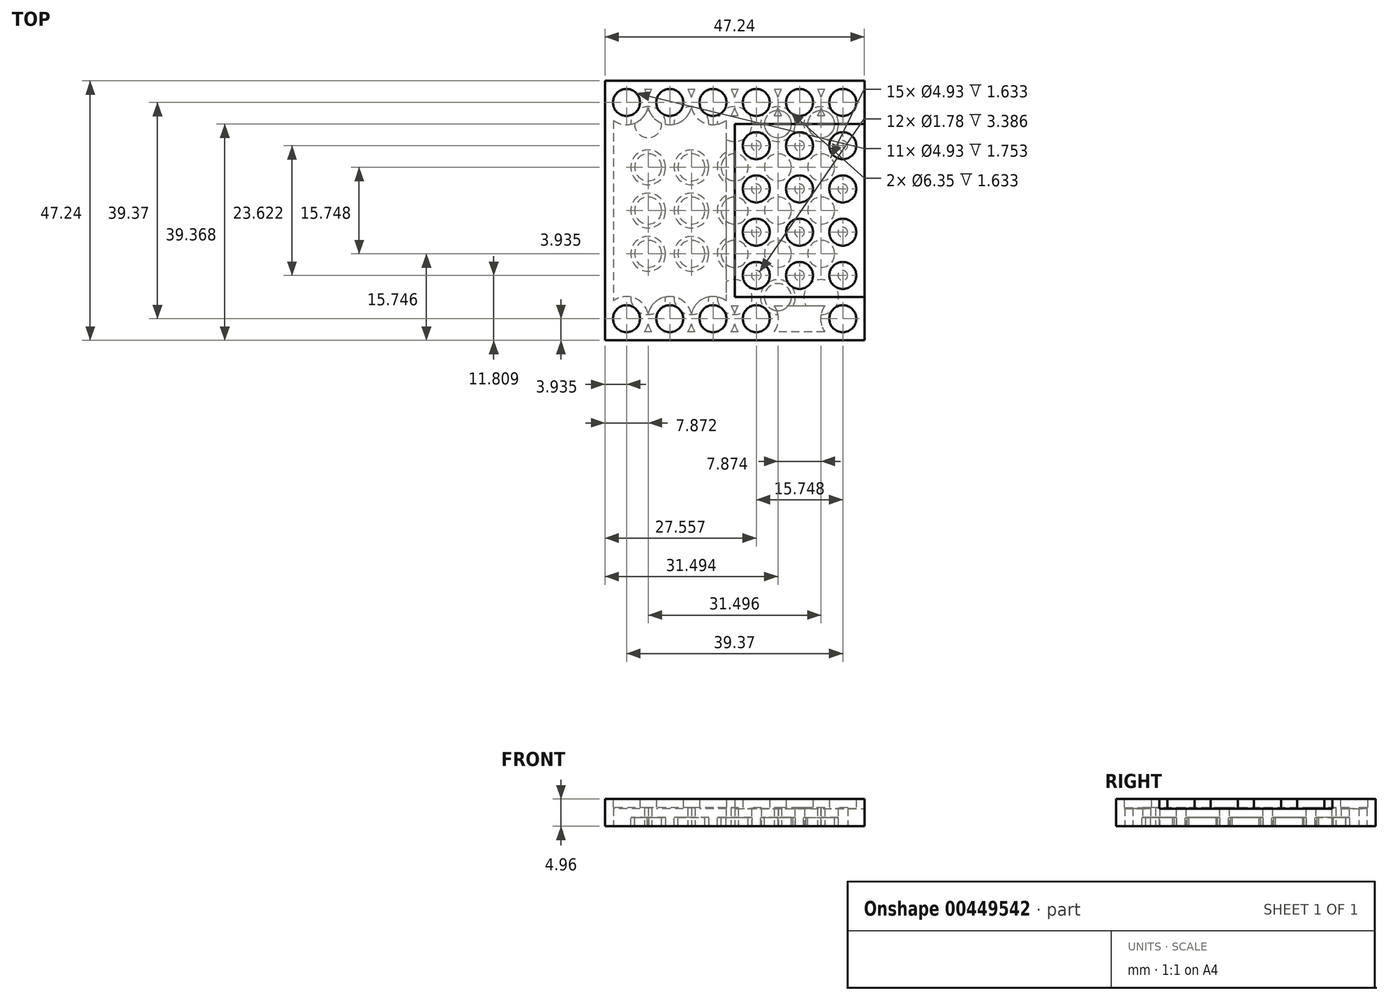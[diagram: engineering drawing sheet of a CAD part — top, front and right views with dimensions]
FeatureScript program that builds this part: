
annotation { "Feature Type Name" : "Feature", "Feature Type Description" : "" }
export const myFeature = defineFeature(function(context is Context, id is Id, definition is map)
    precondition{}
    {
        {
            var Q0;
            Q0=qCreatedBy(makeId("Top.planeOp"),FACE);
            var sketch = newSketch(context, id + "F0", { "sketchPlane" : qUnion([Q0])});
            skLineSegment(sketch, "E0.rect.bottom", {"start": v(23.62, 23.62) * mm, "end": v(-23.62, 23.62) * mm});
            skLineSegment(sketch, "E0.rect.top", {"start": v(23.62, -23.62) * mm, "end": v(-23.62, -23.62) * mm});
            skLineSegment(sketch, "E0.rect.left", {"start": v(23.62, 23.62) * mm, "end": v(23.62, -23.62) * mm});
            skLineSegment(sketch, "E0.rect.right", {"start": v(-23.62, 23.62) * mm, "end": v(-23.62, -23.62) * mm});
            skPoint(sketch, "E0.rect.middle", {"position": v(0, 0) * mm});
            skSolve(sketch);
        }
        {
            var Q0;
            Q0=makeQuery(id+"F0.imprint","IMPRINT",FACE,{"disambiguationData":[TD([[makeQuery(id+"F0.imprint","IMPRINT",EDGE,{"derivedFrom":sQuery(id+"F0.wireOp",EDGE,"E0.rect.bottom")}),1.0]])]});
            extrude(context, id + "F1", {"entities" : qUnion([Q0]), "depth" : 3.2 * mm});
        }
        {
            var Q0;
            Q0=makeQuery(id+"F1.opExtrude","CAP_FACE",FACE,{"disambiguationData":[OSD([sQuery(id+"F0.wireOp",EDGE,"E0.rect.bottom"),sQuery(id+"F0.wireOp",EDGE,"E0.rect.top"),sQuery(id+"F0.wireOp",EDGE,"E0.rect.left"),sQuery(id+"F0.wireOp",EDGE,"E0.rect.right")])],"isStart":false});
            var sketch = newSketch(context, id + "F2", { "sketchPlane" : qUnion([Q0])});
            skLineSegment(sketch, "E1", {"start": v(0, 0) * mm, "end": v(0, 7.87) * mm});
            skLineSegment(sketch, "E2", {"start": v(0, 7.87) * mm, "end": v(0, 15.75) * mm});
            skLineSegment(sketch, "E3", {"start": v(0, 0) * mm, "end": v(0, -7.87) * mm});
            skLineSegment(sketch, "E4", {"start": v(0, -7.87) * mm, "end": v(0, -15.75) * mm});
            skPoint(sketch, "E4.endSnap0", {"position": v(0, -23.62) * mm});
            skLineSegment(sketch, "E5", {"start": v(0, 0) * mm, "end": v(3.94, 0) * mm});
            skLineSegment(sketch, "E6", {"start": v(3.94, 0) * mm, "end": v(11.81, 0) * mm});
            skLineSegment(sketch, "E7", {"start": v(11.81, 0) * mm, "end": v(19.69, 0) * mm});
            skLineSegment(sketch, "E8", {"start": v(0, 0) * mm, "end": v(-3.94, 0) * mm});
            skLineSegment(sketch, "E9", {"start": v(-3.94, 0) * mm, "end": v(-11.81, 0) * mm});
            skLineSegment(sketch, "E10", {"start": v(-11.81, 0) * mm, "end": v(-19.69, 0) * mm});
            skLineSegment(sketch, "E11", {"start": v(-19.69, 0) * mm, "end": v(-19.69, -3.94) * mm});
            skLineSegment(sketch, "E12", {"start": v(-19.69, -3.94) * mm, "end": v(-19.69, -11.81) * mm});
            skLineSegment(sketch, "E13", {"start": v(-19.69, 0) * mm, "end": v(-19.69, 3.94) * mm});
            skLineSegment(sketch, "E14", {"start": v(-19.69, 3.94) * mm, "end": v(-19.69, 11.81) * mm});
            skLineSegment(sketch, "E15", {"start": v(-19.69, 3.94) * mm, "end": v(-11.81, 3.94) * mm});
            skLineSegment(sketch, "E16", {"start": v(-11.81, 3.94) * mm, "end": v(-3.94, 3.94) * mm});
            skLineSegment(sketch, "E17", {"start": v(-3.94, 3.94) * mm, "end": v(-3.94, 11.81) * mm});
            skLineSegment(sketch, "E18", {"start": v(-3.94, 11.81) * mm, "end": v(-11.81, 11.81) * mm});
            skLineSegment(sketch, "E19", {"start": v(-19.69, -3.94) * mm, "end": v(-11.81, -3.94) * mm});
            skLineSegment(sketch, "E20", {"start": v(-11.81, -3.94) * mm, "end": v(-3.94, -3.94) * mm});
            skLineSegment(sketch, "E21", {"start": v(-3.94, -3.94) * mm, "end": v(-3.94, -11.81) * mm});
            skLineSegment(sketch, "E22", {"start": v(-3.94, -11.81) * mm, "end": v(-11.81, -11.81) * mm});
            skLineSegment(sketch, "E23", {"start": v(3.94, 0) * mm, "end": v(3.94, 3.94) * mm});
            skPoint(sketch, "E23.endSnap0", {"position": v(0, 3.94) * mm});
            skLineSegment(sketch, "E24", {"start": v(3.94, 3.94) * mm, "end": v(3.94, 11.81) * mm});
            skPoint(sketch, "E24.endSnap0", {"position": v(0, 11.81) * mm});
            skLineSegment(sketch, "E25", {"start": v(3.94, 11.81) * mm, "end": v(11.81, 11.81) * mm});
            skLineSegment(sketch, "E26", {"start": v(11.81, 11.81) * mm, "end": v(19.69, 11.81) * mm});
            skLineSegment(sketch, "E27", {"start": v(19.69, 11.81) * mm, "end": v(19.69, 3.94) * mm});
            skLineSegment(sketch, "E28", {"start": v(19.69, 3.94) * mm, "end": v(11.81, 3.94) * mm});
            skLineSegment(sketch, "E29", {"start": v(3.94, 0) * mm, "end": v(3.94, -3.94) * mm});
            skPoint(sketch, "E29.endSnap0", {"position": v(0, -3.94) * mm});
            skLineSegment(sketch, "E30", {"start": v(3.94, -3.94) * mm, "end": v(3.94, -11.81) * mm});
            skPoint(sketch, "E30.endSnap0", {"position": v(0, -11.81) * mm});
            skLineSegment(sketch, "E31", {"start": v(3.94, -11.81) * mm, "end": v(11.81, -11.81) * mm});
            skLineSegment(sketch, "E32", {"start": v(11.81, -11.81) * mm, "end": v(19.69, -11.81) * mm});
            skLineSegment(sketch, "E33", {"start": v(19.69, -11.81) * mm, "end": v(19.69, -3.94) * mm});
            skLineSegment(sketch, "E34", {"start": v(19.69, -3.94) * mm, "end": v(11.81, -3.94) * mm});
            skCircle(sketch, "E35", {"center": v(-19.69, 11.81) * mm, "radius": 2.46 * mm});
            skCircle(sketch, "E36", {"center": v(-11.81, 11.81) * mm, "radius": 2.46 * mm});
            skCircle(sketch, "E37", {"center": v(-3.94, 11.81) * mm, "radius": 2.46 * mm});
            skCircle(sketch, "E38", {"center": v(3.94, 11.81) * mm, "radius": 2.46 * mm});
            skCircle(sketch, "E39", {"center": v(11.81, 11.81) * mm, "radius": 2.46 * mm});
            skCircle(sketch, "E40", {"center": v(19.69, 11.81) * mm, "radius": 2.46 * mm});
            skCircle(sketch, "E41", {"center": v(19.69, 3.94) * mm, "radius": 2.46 * mm});
            skCircle(sketch, "E42", {"center": v(11.81, 3.94) * mm, "radius": 2.46 * mm});
            skCircle(sketch, "E43", {"center": v(3.94, 3.94) * mm, "radius": 2.46 * mm});
            skCircle(sketch, "E44", {"center": v(-3.94, 3.94) * mm, "radius": 2.46 * mm});
            skCircle(sketch, "E45", {"center": v(-11.81, 3.94) * mm, "radius": 2.46 * mm});
            skCircle(sketch, "E46", {"center": v(-19.69, 3.94) * mm, "radius": 2.46 * mm});
            skCircle(sketch, "E47", {"center": v(-19.69, -3.94) * mm, "radius": 2.46 * mm});
            skCircle(sketch, "E48", {"center": v(-11.81, -3.94) * mm, "radius": 2.46 * mm});
            skCircle(sketch, "E49", {"center": v(-3.94, -3.94) * mm, "radius": 2.46 * mm});
            skCircle(sketch, "E50", {"center": v(-3.94, -11.81) * mm, "radius": 2.46 * mm});
            skCircle(sketch, "E51", {"center": v(-11.81, -11.81) * mm, "radius": 2.46 * mm});
            skCircle(sketch, "E52", {"center": v(-19.69, -11.81) * mm, "radius": 2.46 * mm});
            skCircle(sketch, "E53", {"center": v(3.94, -11.81) * mm, "radius": 2.46 * mm});
            skCircle(sketch, "E54", {"center": v(11.81, -11.81) * mm, "radius": 2.46 * mm});
            skCircle(sketch, "E55", {"center": v(19.69, -11.81) * mm, "radius": 2.46 * mm});
            skCircle(sketch, "E56", {"center": v(19.69, -3.94) * mm, "radius": 2.46 * mm});
            skCircle(sketch, "E57", {"center": v(11.81, -3.94) * mm, "radius": 2.46 * mm});
            skCircle(sketch, "E58", {"center": v(3.94, -3.94) * mm, "radius": 2.46 * mm});
            skLineSegment(sketch, "E59", {"start": v(0, -15.75) * mm, "end": v(23.62, -15.75) * mm});
            skLineSegment(sketch, "E60.MirrorCS", {"start": v(3.94, -19.69) * mm, "end": v(11.81, -19.69) * mm});
            skCircle(sketch, "E61.MirrorC", {"center": v(-11.81, -19.68) * mm, "radius": 2.46 * mm});
            skPoint(sketch, "E62.MirrorP", {"position": v(0, -19.69) * mm});
            skCircle(sketch, "E63.MirrorC", {"center": v(-3.94, -19.69) * mm, "radius": 2.46 * mm});
            skCircle(sketch, "E64.MirrorC", {"center": v(11.81, -19.69) * mm, "radius": 2.46 * mm});
            skLineSegment(sketch, "E65.MirrorCS", {"start": v(11.81, -19.69) * mm, "end": v(19.69, -19.69) * mm});
            skLineSegment(sketch, "E66.MirrorCS", {"start": v(-3.94, -19.68) * mm, "end": v(-11.81, -19.68) * mm});
            skCircle(sketch, "E67.MirrorC", {"center": v(19.69, -19.69) * mm, "radius": 2.46 * mm});
            skCircle(sketch, "E68.MirrorC", {"center": v(3.94, -19.69) * mm, "radius": 2.46 * mm});
            skCircle(sketch, "E69.MirrorC", {"center": v(-19.69, -19.69) * mm, "radius": 2.46 * mm});
            skLineSegment(sketch, "E70", {"start": v(0, 15.75) * mm, "end": v(23.62, 15.75) * mm});
            skCircle(sketch, "E71.MirrorC", {"center": v(-3.94, 19.69) * mm, "radius": 2.46 * mm});
            skCircle(sketch, "E72.MirrorC", {"center": v(3.94, 19.69) * mm, "radius": 2.46 * mm});
            skCircle(sketch, "E73.MirrorC", {"center": v(-11.81, 19.69) * mm, "radius": 2.46 * mm});
            skCircle(sketch, "E74.MirrorC", {"center": v(11.81, 19.69) * mm, "radius": 2.46 * mm});
            skCircle(sketch, "E75.MirrorC", {"center": v(-19.69, 19.69) * mm, "radius": 2.46 * mm});
            skPoint(sketch, "E76.MirrorP", {"position": v(0, 19.69) * mm});
            skCircle(sketch, "E77.MirrorC", {"center": v(19.69, 19.69) * mm, "radius": 2.46 * mm});
            skSolve(sketch);
        }
        {
            var Q0;
            Q0=makeQuery(id+"F2.imprint","IMPRINT",FACE,{"disambiguationData":[TD([[makeQuery(id+"F2.imprint","IMPRINT",EDGE,{"derivedFrom":sQuery(id+"F2.wireOp",EDGE,"E35")}),1.0]])]});
            var Q1;
            Q1=makeQuery(id+"F2.imprint","IMPRINT",FACE,{"disambiguationData":[TD([[makeQuery(id+"F2.imprint","IMPRINT",EDGE,{"derivedFrom":sQuery(id+"F2.wireOp",EDGE,"E36")}),1.0]])]});
            var Q2;
            {var subQ0=sQuery(id+"F2.wireOp",EDGE,"E18");var subQ1=sQuery(id+"F2.wireOp",EDGE,"E17");var subQ2=makeQuery(id+"F2.imprint","INTERSECT",VERTEX,{"derivedFrom":[subQ1,subQ0]});Q2=makeQuery(id+"F2.imprint","IMPRINT",FACE,{"disambiguationData":[TD([[makeQuery(id+"F2.imprint","IMPRINT",EDGE,{"disambiguationData":[TD([[subQ2,1.0]])],"derivedFrom":subQ1}),-1.0]])]});}
            var Q3;
            {var subQ0=sQuery(id+"F2.wireOp",EDGE,"E18");var subQ1=sQuery(id+"F2.wireOp",EDGE,"E17");var subQ2=makeQuery(id+"F2.imprint","INTERSECT",VERTEX,{"derivedFrom":[subQ1,subQ0]});Q3=makeQuery(id+"F2.imprint","IMPRINT",FACE,{"disambiguationData":[TD([[makeQuery(id+"F2.imprint","IMPRINT",EDGE,{"disambiguationData":[TD([[subQ2,1.0]])],"derivedFrom":subQ1}),1.0]])]});}
            var Q4;
            {var subQ0=sQuery(id+"F2.wireOp",EDGE,"E25");var subQ1=sQuery(id+"F2.wireOp",EDGE,"E24");var subQ2=makeQuery(id+"F2.imprint","INTERSECT",VERTEX,{"derivedFrom":[subQ1,subQ0]});Q4=makeQuery(id+"F2.imprint","IMPRINT",FACE,{"disambiguationData":[TD([[makeQuery(id+"F2.imprint","IMPRINT",EDGE,{"disambiguationData":[TD([[subQ2,1.0]])],"derivedFrom":subQ1}),1.0]])]});}
            var Q5;
            {var subQ0=sQuery(id+"F2.wireOp",EDGE,"E25");var subQ1=sQuery(id+"F2.wireOp",EDGE,"E24");var subQ2=makeQuery(id+"F2.imprint","INTERSECT",VERTEX,{"derivedFrom":[subQ1,subQ0]});Q5=makeQuery(id+"F2.imprint","IMPRINT",FACE,{"disambiguationData":[TD([[makeQuery(id+"F2.imprint","IMPRINT",EDGE,{"disambiguationData":[TD([[subQ2,1.0]])],"derivedFrom":subQ1}),-1.0]])]});}
            var Q6;
            {var subQ0=sQuery(id+"F2.wireOp",EDGE,"E24");var subQ1=sQuery(id+"F2.wireOp",EDGE,"E23");var subQ2=makeQuery(id+"F2.imprint","INTERSECT",VERTEX,{"derivedFrom":[subQ1,subQ0]});Q6=makeQuery(id+"F2.imprint","IMPRINT",FACE,{"disambiguationData":[TD([[makeQuery(id+"F2.imprint","IMPRINT",EDGE,{"disambiguationData":[TD([[subQ2,1.0]])],"derivedFrom":subQ1}),-1.0]])]});}
            var Q7;
            {var subQ0=sQuery(id+"F2.wireOp",EDGE,"E24");var subQ1=sQuery(id+"F2.wireOp",EDGE,"E23");var subQ2=makeQuery(id+"F2.imprint","INTERSECT",VERTEX,{"derivedFrom":[subQ1,subQ0]});Q7=makeQuery(id+"F2.imprint","IMPRINT",FACE,{"disambiguationData":[TD([[makeQuery(id+"F2.imprint","IMPRINT",EDGE,{"disambiguationData":[TD([[subQ2,1.0]])],"derivedFrom":subQ1}),1.0]])]});}
            var Q8;
            {var subQ0=sQuery(id+"F2.wireOp",EDGE,"E17");var subQ1=sQuery(id+"F2.wireOp",EDGE,"E16");var subQ2=makeQuery(id+"F2.imprint","INTERSECT",VERTEX,{"derivedFrom":[subQ1,subQ0]});Q8=makeQuery(id+"F2.imprint","IMPRINT",FACE,{"disambiguationData":[TD([[makeQuery(id+"F2.imprint","IMPRINT",EDGE,{"disambiguationData":[TD([[subQ2,1.0]])],"derivedFrom":subQ1}),-1.0]])]});}
            var Q9;
            {var subQ0=sQuery(id+"F2.wireOp",EDGE,"E17");var subQ1=sQuery(id+"F2.wireOp",EDGE,"E16");var subQ2=makeQuery(id+"F2.imprint","INTERSECT",VERTEX,{"derivedFrom":[subQ1,subQ0]});Q9=makeQuery(id+"F2.imprint","IMPRINT",FACE,{"disambiguationData":[TD([[makeQuery(id+"F2.imprint","IMPRINT",EDGE,{"disambiguationData":[TD([[subQ2,1.0]])],"derivedFrom":subQ1}),1.0]])]});}
            var Q10;
            {var subQ0=sQuery(id+"F2.wireOp",EDGE,"E16");var subQ1=sQuery(id+"F2.wireOp",EDGE,"E15");var subQ2=makeQuery(id+"F2.imprint","INTERSECT",VERTEX,{"derivedFrom":[subQ1,subQ0]});Q10=makeQuery(id+"F2.imprint","IMPRINT",FACE,{"disambiguationData":[TD([[makeQuery(id+"F2.imprint","IMPRINT",EDGE,{"disambiguationData":[TD([[subQ2,1.0]])],"derivedFrom":subQ1}),1.0]])]});}
            var Q11;
            {var subQ0=sQuery(id+"F2.wireOp",EDGE,"E16");var subQ1=sQuery(id+"F2.wireOp",EDGE,"E15");var subQ2=makeQuery(id+"F2.imprint","INTERSECT",VERTEX,{"derivedFrom":[subQ1,subQ0]});Q11=makeQuery(id+"F2.imprint","IMPRINT",FACE,{"disambiguationData":[TD([[makeQuery(id+"F2.imprint","IMPRINT",EDGE,{"disambiguationData":[TD([[subQ2,1.0]])],"derivedFrom":subQ1}),-1.0]])]});}
            var Q12;
            {var subQ1=sQuery(id+"F2.wireOp",EDGE,"E14");var subQ3=sQuery(id+"F2.wireOp",EDGE,"E46");var subQ4=makeQuery(id+"F2.imprint","INTERSECT",VERTEX,{"derivedFrom":[subQ1,subQ3]});Q12=makeQuery(id+"F2.imprint","IMPRINT",FACE,{"disambiguationData":[TD([[makeQuery(id+"F2.imprint","IMPRINT",EDGE,{"disambiguationData":[TD([[subQ4,1.0]])],"derivedFrom":subQ3}),1.0]])]});}
            var Q13;
            {var subQ1=sQuery(id+"F2.wireOp",EDGE,"E13");var subQ3=sQuery(id+"F2.wireOp",EDGE,"E46");var subQ4=makeQuery(id+"F2.imprint","INTERSECT",VERTEX,{"derivedFrom":[subQ1,subQ3]});Q13=makeQuery(id+"F2.imprint","IMPRINT",FACE,{"disambiguationData":[TD([[makeQuery(id+"F2.imprint","IMPRINT",EDGE,{"disambiguationData":[TD([[subQ4,-1.0]])],"derivedFrom":subQ3}),1.0]])]});}
            var Q14;
            {var subQ1=sQuery(id+"F2.wireOp",EDGE,"E13");var subQ3=sQuery(id+"F2.wireOp",EDGE,"E46");var subQ4=makeQuery(id+"F2.imprint","INTERSECT",VERTEX,{"derivedFrom":[subQ1,subQ3]});Q14=makeQuery(id+"F2.imprint","IMPRINT",FACE,{"disambiguationData":[TD([[makeQuery(id+"F2.imprint","IMPRINT",EDGE,{"disambiguationData":[TD([[subQ4,1.0]])],"derivedFrom":subQ3}),1.0]])]});}
            var Q15;
            {var subQ1=sQuery(id+"F2.wireOp",EDGE,"E11");var subQ3=sQuery(id+"F2.wireOp",EDGE,"E47");var subQ4=makeQuery(id+"F2.imprint","INTERSECT",VERTEX,{"derivedFrom":[subQ1,subQ3]});Q15=makeQuery(id+"F2.imprint","IMPRINT",FACE,{"disambiguationData":[TD([[makeQuery(id+"F2.imprint","IMPRINT",EDGE,{"disambiguationData":[TD([[subQ4,1.0]])],"derivedFrom":subQ3}),1.0]])]});}
            var Q16;
            {var subQ1=sQuery(id+"F2.wireOp",EDGE,"E12");var subQ3=sQuery(id+"F2.wireOp",EDGE,"E47");var subQ4=makeQuery(id+"F2.imprint","INTERSECT",VERTEX,{"derivedFrom":[subQ1,subQ3]});Q16=makeQuery(id+"F2.imprint","IMPRINT",FACE,{"disambiguationData":[TD([[makeQuery(id+"F2.imprint","IMPRINT",EDGE,{"disambiguationData":[TD([[subQ4,-1.0]])],"derivedFrom":subQ3}),1.0]])]});}
            var Q17;
            {var subQ1=sQuery(id+"F2.wireOp",EDGE,"E11");var subQ3=sQuery(id+"F2.wireOp",EDGE,"E47");var subQ4=makeQuery(id+"F2.imprint","INTERSECT",VERTEX,{"derivedFrom":[subQ1,subQ3]});Q17=makeQuery(id+"F2.imprint","IMPRINT",FACE,{"disambiguationData":[TD([[makeQuery(id+"F2.imprint","IMPRINT",EDGE,{"disambiguationData":[TD([[subQ4,-1.0]])],"derivedFrom":subQ3}),1.0]])]});}
            var Q18;
            {var subQ0=sQuery(id+"F2.wireOp",EDGE,"E20");var subQ1=sQuery(id+"F2.wireOp",EDGE,"E19");var subQ2=makeQuery(id+"F2.imprint","INTERSECT",VERTEX,{"derivedFrom":[subQ1,subQ0]});Q18=makeQuery(id+"F2.imprint","IMPRINT",FACE,{"disambiguationData":[TD([[makeQuery(id+"F2.imprint","IMPRINT",EDGE,{"disambiguationData":[TD([[subQ2,1.0]])],"derivedFrom":subQ1}),1.0]])]});}
            var Q19;
            {var subQ0=sQuery(id+"F2.wireOp",EDGE,"E20");var subQ1=sQuery(id+"F2.wireOp",EDGE,"E19");var subQ2=makeQuery(id+"F2.imprint","INTERSECT",VERTEX,{"derivedFrom":[subQ1,subQ0]});Q19=makeQuery(id+"F2.imprint","IMPRINT",FACE,{"disambiguationData":[TD([[makeQuery(id+"F2.imprint","IMPRINT",EDGE,{"disambiguationData":[TD([[subQ2,1.0]])],"derivedFrom":subQ1}),-1.0]])]});}
            var Q20;
            {var subQ0=sQuery(id+"F2.wireOp",EDGE,"E21");var subQ1=sQuery(id+"F2.wireOp",EDGE,"E20");var subQ2=makeQuery(id+"F2.imprint","INTERSECT",VERTEX,{"derivedFrom":[subQ1,subQ0]});Q20=makeQuery(id+"F2.imprint","IMPRINT",FACE,{"disambiguationData":[TD([[makeQuery(id+"F2.imprint","IMPRINT",EDGE,{"disambiguationData":[TD([[subQ2,1.0]])],"derivedFrom":subQ1}),-1.0]])]});}
            var Q21;
            {var subQ0=sQuery(id+"F2.wireOp",EDGE,"E21");var subQ1=sQuery(id+"F2.wireOp",EDGE,"E20");var subQ2=makeQuery(id+"F2.imprint","INTERSECT",VERTEX,{"derivedFrom":[subQ1,subQ0]});Q21=makeQuery(id+"F2.imprint","IMPRINT",FACE,{"disambiguationData":[TD([[makeQuery(id+"F2.imprint","IMPRINT",EDGE,{"disambiguationData":[TD([[subQ2,1.0]])],"derivedFrom":subQ1}),1.0]])]});}
            var Q22;
            {var subQ0=sQuery(id+"F2.wireOp",EDGE,"E22");var subQ1=sQuery(id+"F2.wireOp",EDGE,"E21");var subQ2=makeQuery(id+"F2.imprint","INTERSECT",VERTEX,{"derivedFrom":[subQ1,subQ0]});Q22=makeQuery(id+"F2.imprint","IMPRINT",FACE,{"disambiguationData":[TD([[makeQuery(id+"F2.imprint","IMPRINT",EDGE,{"disambiguationData":[TD([[subQ2,1.0]])],"derivedFrom":subQ1}),1.0]])]});}
            var Q23;
            {var subQ0=sQuery(id+"F2.wireOp",EDGE,"E22");var subQ1=sQuery(id+"F2.wireOp",EDGE,"E21");var subQ2=makeQuery(id+"F2.imprint","INTERSECT",VERTEX,{"derivedFrom":[subQ1,subQ0]});Q23=makeQuery(id+"F2.imprint","IMPRINT",FACE,{"disambiguationData":[TD([[makeQuery(id+"F2.imprint","IMPRINT",EDGE,{"disambiguationData":[TD([[subQ2,1.0]])],"derivedFrom":subQ1}),-1.0]])]});}
            var Q24;
            Q24=makeQuery(id+"F2.imprint","IMPRINT",FACE,{"disambiguationData":[TD([[makeQuery(id+"F2.imprint","IMPRINT",EDGE,{"derivedFrom":sQuery(id+"F2.wireOp",EDGE,"E51")}),1.0]])]});
            var Q25;
            Q25=makeQuery(id+"F2.imprint","IMPRINT",FACE,{"disambiguationData":[TD([[makeQuery(id+"F2.imprint","IMPRINT",EDGE,{"derivedFrom":sQuery(id+"F2.wireOp",EDGE,"E52")}),1.0]])]});
            var Q26;
            {var subQ0=sQuery(id+"F2.wireOp",EDGE,"E31");var subQ1=sQuery(id+"F2.wireOp",EDGE,"E30");var subQ2=makeQuery(id+"F2.imprint","INTERSECT",VERTEX,{"derivedFrom":[subQ1,subQ0]});Q26=makeQuery(id+"F2.imprint","IMPRINT",FACE,{"disambiguationData":[TD([[makeQuery(id+"F2.imprint","IMPRINT",EDGE,{"disambiguationData":[TD([[subQ2,1.0]])],"derivedFrom":subQ1}),-1.0]])]});}
            var Q27;
            {var subQ0=sQuery(id+"F2.wireOp",EDGE,"E31");var subQ1=sQuery(id+"F2.wireOp",EDGE,"E30");var subQ2=makeQuery(id+"F2.imprint","INTERSECT",VERTEX,{"derivedFrom":[subQ1,subQ0]});Q27=makeQuery(id+"F2.imprint","IMPRINT",FACE,{"disambiguationData":[TD([[makeQuery(id+"F2.imprint","IMPRINT",EDGE,{"disambiguationData":[TD([[subQ2,1.0]])],"derivedFrom":subQ1}),1.0]])]});}
            var Q28;
            {var subQ0=sQuery(id+"F2.wireOp",EDGE,"E30");var subQ1=sQuery(id+"F2.wireOp",EDGE,"E29");var subQ2=makeQuery(id+"F2.imprint","INTERSECT",VERTEX,{"derivedFrom":[subQ1,subQ0]});Q28=makeQuery(id+"F2.imprint","IMPRINT",FACE,{"disambiguationData":[TD([[makeQuery(id+"F2.imprint","IMPRINT",EDGE,{"disambiguationData":[TD([[subQ2,1.0]])],"derivedFrom":subQ1}),1.0]])]});}
            var Q29;
            {var subQ0=sQuery(id+"F2.wireOp",EDGE,"E30");var subQ1=sQuery(id+"F2.wireOp",EDGE,"E29");var subQ2=makeQuery(id+"F2.imprint","INTERSECT",VERTEX,{"derivedFrom":[subQ1,subQ0]});Q29=makeQuery(id+"F2.imprint","IMPRINT",FACE,{"disambiguationData":[TD([[makeQuery(id+"F2.imprint","IMPRINT",EDGE,{"disambiguationData":[TD([[subQ2,1.0]])],"derivedFrom":subQ1}),-1.0]])]});}
            var Q30;
            Q30=makeQuery(id+"F2.imprint","IMPRINT",FACE,{"disambiguationData":[TD([[makeQuery(id+"F2.imprint","IMPRINT",EDGE,{"derivedFrom":sQuery(id+"F2.wireOp",EDGE,"E57")}),1.0]])]});
            var Q31;
            {var subQ0=sQuery(id+"F2.wireOp",EDGE,"E34");var subQ1=sQuery(id+"F2.wireOp",EDGE,"E33");var subQ2=makeQuery(id+"F2.imprint","INTERSECT",VERTEX,{"derivedFrom":[subQ1,subQ0]});Q31=makeQuery(id+"F2.imprint","IMPRINT",FACE,{"disambiguationData":[TD([[makeQuery(id+"F2.imprint","IMPRINT",EDGE,{"disambiguationData":[TD([[subQ2,1.0]])],"derivedFrom":subQ1}),-1.0]])]});}
            var Q32;
            {var subQ0=sQuery(id+"F2.wireOp",EDGE,"E34");var subQ1=sQuery(id+"F2.wireOp",EDGE,"E33");var subQ2=makeQuery(id+"F2.imprint","INTERSECT",VERTEX,{"derivedFrom":[subQ1,subQ0]});Q32=makeQuery(id+"F2.imprint","IMPRINT",FACE,{"disambiguationData":[TD([[makeQuery(id+"F2.imprint","IMPRINT",EDGE,{"disambiguationData":[TD([[subQ2,1.0]])],"derivedFrom":subQ1}),1.0]])]});}
            var Q33;
            {var subQ0=sQuery(id+"F2.wireOp",EDGE,"E33");var subQ1=sQuery(id+"F2.wireOp",EDGE,"E32");var subQ2=makeQuery(id+"F2.imprint","INTERSECT",VERTEX,{"derivedFrom":[subQ1,subQ0]});Q33=makeQuery(id+"F2.imprint","IMPRINT",FACE,{"disambiguationData":[TD([[makeQuery(id+"F2.imprint","IMPRINT",EDGE,{"disambiguationData":[TD([[subQ2,1.0]])],"derivedFrom":subQ1}),-1.0]])]});}
            var Q34;
            {var subQ0=sQuery(id+"F2.wireOp",EDGE,"E33");var subQ1=sQuery(id+"F2.wireOp",EDGE,"E32");var subQ2=makeQuery(id+"F2.imprint","INTERSECT",VERTEX,{"derivedFrom":[subQ1,subQ0]});Q34=makeQuery(id+"F2.imprint","IMPRINT",FACE,{"disambiguationData":[TD([[makeQuery(id+"F2.imprint","IMPRINT",EDGE,{"disambiguationData":[TD([[subQ2,1.0]])],"derivedFrom":subQ1}),1.0]])]});}
            var Q35;
            {var subQ0=sQuery(id+"F2.wireOp",EDGE,"E32");var subQ1=sQuery(id+"F2.wireOp",EDGE,"E31");var subQ2=makeQuery(id+"F2.imprint","INTERSECT",VERTEX,{"derivedFrom":[subQ1,subQ0]});Q35=makeQuery(id+"F2.imprint","IMPRINT",FACE,{"disambiguationData":[TD([[makeQuery(id+"F2.imprint","IMPRINT",EDGE,{"disambiguationData":[TD([[subQ2,1.0]])],"derivedFrom":subQ1}),1.0]])]});}
            var Q36;
            {var subQ0=sQuery(id+"F2.wireOp",EDGE,"E32");var subQ1=sQuery(id+"F2.wireOp",EDGE,"E31");var subQ2=makeQuery(id+"F2.imprint","INTERSECT",VERTEX,{"derivedFrom":[subQ1,subQ0]});Q36=makeQuery(id+"F2.imprint","IMPRINT",FACE,{"disambiguationData":[TD([[makeQuery(id+"F2.imprint","IMPRINT",EDGE,{"disambiguationData":[TD([[subQ2,1.0]])],"derivedFrom":subQ1}),-1.0]])]});}
            var Q37;
            {var subQ0=sQuery(id+"F2.wireOp",EDGE,"E28");var subQ1=sQuery(id+"F2.wireOp",EDGE,"E27");var subQ2=makeQuery(id+"F2.imprint","INTERSECT",VERTEX,{"derivedFrom":[subQ1,subQ0]});Q37=makeQuery(id+"F2.imprint","IMPRINT",FACE,{"disambiguationData":[TD([[makeQuery(id+"F2.imprint","IMPRINT",EDGE,{"disambiguationData":[TD([[subQ2,1.0]])],"derivedFrom":subQ1}),1.0]])]});}
            var Q38;
            {var subQ0=sQuery(id+"F2.wireOp",EDGE,"E28");var subQ1=sQuery(id+"F2.wireOp",EDGE,"E27");var subQ2=makeQuery(id+"F2.imprint","INTERSECT",VERTEX,{"derivedFrom":[subQ1,subQ0]});Q38=makeQuery(id+"F2.imprint","IMPRINT",FACE,{"disambiguationData":[TD([[makeQuery(id+"F2.imprint","IMPRINT",EDGE,{"disambiguationData":[TD([[subQ2,1.0]])],"derivedFrom":subQ1}),-1.0]])]});}
            var Q39;
            Q39=makeQuery(id+"F2.imprint","IMPRINT",FACE,{"disambiguationData":[TD([[makeQuery(id+"F2.imprint","IMPRINT",EDGE,{"derivedFrom":sQuery(id+"F2.wireOp",EDGE,"E42")}),1.0]])]});
            var Q40;
            {var subQ0=sQuery(id+"F2.wireOp",EDGE,"E26");var subQ1=sQuery(id+"F2.wireOp",EDGE,"E25");var subQ2=makeQuery(id+"F2.imprint","INTERSECT",VERTEX,{"derivedFrom":[subQ1,subQ0]});Q40=makeQuery(id+"F2.imprint","IMPRINT",FACE,{"disambiguationData":[TD([[makeQuery(id+"F2.imprint","IMPRINT",EDGE,{"disambiguationData":[TD([[subQ2,1.0]])],"derivedFrom":subQ1}),-1.0]])]});}
            var Q41;
            {var subQ0=sQuery(id+"F2.wireOp",EDGE,"E26");var subQ1=sQuery(id+"F2.wireOp",EDGE,"E25");var subQ2=makeQuery(id+"F2.imprint","INTERSECT",VERTEX,{"derivedFrom":[subQ1,subQ0]});Q41=makeQuery(id+"F2.imprint","IMPRINT",FACE,{"disambiguationData":[TD([[makeQuery(id+"F2.imprint","IMPRINT",EDGE,{"disambiguationData":[TD([[subQ2,1.0]])],"derivedFrom":subQ1}),1.0]])]});}
            var Q42;
            {var subQ0=sQuery(id+"F2.wireOp",EDGE,"E27");var subQ1=sQuery(id+"F2.wireOp",EDGE,"E26");var subQ2=makeQuery(id+"F2.imprint","INTERSECT",VERTEX,{"derivedFrom":[subQ1,subQ0]});Q42=makeQuery(id+"F2.imprint","IMPRINT",FACE,{"disambiguationData":[TD([[makeQuery(id+"F2.imprint","IMPRINT",EDGE,{"disambiguationData":[TD([[subQ2,1.0]])],"derivedFrom":subQ1}),1.0]])]});}
            var Q43;
            {var subQ0=sQuery(id+"F2.wireOp",EDGE,"E27");var subQ1=sQuery(id+"F2.wireOp",EDGE,"E26");var subQ2=makeQuery(id+"F2.imprint","INTERSECT",VERTEX,{"derivedFrom":[subQ1,subQ0]});Q43=makeQuery(id+"F2.imprint","IMPRINT",FACE,{"disambiguationData":[TD([[makeQuery(id+"F2.imprint","IMPRINT",EDGE,{"disambiguationData":[TD([[subQ2,1.0]])],"derivedFrom":subQ1}),-1.0]])]});}
            var Q44;
            Q44=makeQuery(id+"F2.imprint","IMPRINT",FACE,{"disambiguationData":[TD([[makeQuery(id+"F2.imprint","IMPRINT",EDGE,{"derivedFrom":sQuery(id+"F2.wireOp",EDGE,"E69.MirrorC")}),-1.0]])]});
            var Q45;
            Q45=makeQuery(id+"F2.imprint","IMPRINT",FACE,{"disambiguationData":[TD([[makeQuery(id+"F2.imprint","IMPRINT",EDGE,{"derivedFrom":sQuery(id+"F2.wireOp",EDGE,"E61.MirrorC")}),-1.0]])]});
            var Q46;
            Q46=makeQuery(id+"F2.imprint","IMPRINT",FACE,{"disambiguationData":[TD([[makeQuery(id+"F2.imprint","IMPRINT",EDGE,{"derivedFrom":sQuery(id+"F2.wireOp",EDGE,"E63.MirrorC")}),-1.0]])]});
            var Q47;
            Q47=makeQuery(id+"F2.imprint","IMPRINT",FACE,{"disambiguationData":[TD([[makeQuery(id+"F2.imprint","IMPRINT",EDGE,{"derivedFrom":sQuery(id+"F2.wireOp",EDGE,"E68.MirrorC")}),-1.0]])]});
            var Q48;
            {var subQ0=sQuery(id+"F2.wireOp",EDGE,"E65.MirrorCS");var subQ1=sQuery(id+"F2.wireOp",EDGE,"E60.MirrorCS");var subQ2=makeQuery(id+"F2.imprint","INTERSECT",VERTEX,{"derivedFrom":[subQ1,subQ0]});Q48=makeQuery(id+"F2.imprint","IMPRINT",FACE,{"disambiguationData":[TD([[makeQuery(id+"F2.imprint","IMPRINT",EDGE,{"disambiguationData":[TD([[subQ2,1.0]])],"derivedFrom":subQ1}),1.0]])]});}
            var Q49;
            {var subQ0=sQuery(id+"F2.wireOp",EDGE,"E65.MirrorCS");var subQ1=sQuery(id+"F2.wireOp",EDGE,"E60.MirrorCS");var subQ2=makeQuery(id+"F2.imprint","INTERSECT",VERTEX,{"derivedFrom":[subQ1,subQ0]});Q49=makeQuery(id+"F2.imprint","IMPRINT",FACE,{"disambiguationData":[TD([[makeQuery(id+"F2.imprint","IMPRINT",EDGE,{"disambiguationData":[TD([[subQ2,1.0]])],"derivedFrom":subQ1}),-1.0]])]});}
            var Q50;
            Q50=makeQuery(id+"F2.imprint","IMPRINT",FACE,{"disambiguationData":[TD([[makeQuery(id+"F2.imprint","IMPRINT",EDGE,{"derivedFrom":sQuery(id+"F2.wireOp",EDGE,"E67.MirrorC")}),-1.0]])]});
            var Q51;
            Q51=makeQuery(id+"F2.imprint","IMPRINT",FACE,{"disambiguationData":[TD([[makeQuery(id+"F2.imprint","IMPRINT",EDGE,{"derivedFrom":sQuery(id+"F2.wireOp",EDGE,"E77.MirrorC")}),-1.0]])]});
            var Q52;
            Q52=makeQuery(id+"F2.imprint","IMPRINT",FACE,{"disambiguationData":[TD([[makeQuery(id+"F2.imprint","IMPRINT",EDGE,{"derivedFrom":sQuery(id+"F2.wireOp",EDGE,"E74.MirrorC")}),-1.0]])]});
            var Q53;
            Q53=makeQuery(id+"F2.imprint","IMPRINT",FACE,{"disambiguationData":[TD([[makeQuery(id+"F2.imprint","IMPRINT",EDGE,{"derivedFrom":sQuery(id+"F2.wireOp",EDGE,"E72.MirrorC")}),-1.0]])]});
            var Q54;
            Q54=makeQuery(id+"F2.imprint","IMPRINT",FACE,{"disambiguationData":[TD([[makeQuery(id+"F2.imprint","IMPRINT",EDGE,{"derivedFrom":sQuery(id+"F2.wireOp",EDGE,"E71.MirrorC")}),-1.0]])]});
            var Q55;
            Q55=makeQuery(id+"F2.imprint","IMPRINT",FACE,{"disambiguationData":[TD([[makeQuery(id+"F2.imprint","IMPRINT",EDGE,{"derivedFrom":sQuery(id+"F2.wireOp",EDGE,"E73.MirrorC")}),-1.0]])]});
            var Q56;
            Q56=makeQuery(id+"F2.imprint","IMPRINT",FACE,{"disambiguationData":[TD([[makeQuery(id+"F2.imprint","IMPRINT",EDGE,{"derivedFrom":sQuery(id+"F2.wireOp",EDGE,"E75.MirrorC")}),-1.0]])]});
            extrude(context, id + "F3", {"entities" : qUnion([Q0, Q1, Q2, Q3, Q4, Q5, Q6, Q7, Q8, Q9, Q10, Q11, Q12, Q13, Q14, Q15, Q16, Q17, Q18, Q19, Q20, Q21, Q22, Q23, Q24, Q25, Q26, Q27, Q28, Q29, Q30, Q31, Q32, Q33, Q34, Q35, Q36, Q37, Q38, Q39, Q40, Q41, Q42, Q43, Q44, Q45, Q46, Q47, Q48, Q49, Q50, Q51, Q52, Q53, Q54, Q55, Q56]), "operationType" : NewBodyOperationType.ADD, "depth" : 1.75 * mm});
        }
        {
            var Q0;
            Q0=makeQuery(id+"F1.opExtrude","CAP_FACE",FACE,{"disambiguationData":[OSD([sQuery(id+"F0.wireOp",EDGE,"E0.rect.bottom"),sQuery(id+"F0.wireOp",EDGE,"E0.rect.top"),sQuery(id+"F0.wireOp",EDGE,"E0.rect.left"),sQuery(id+"F0.wireOp",EDGE,"E0.rect.right")])],"isStart":true});
            shell(context, id + "F4", {"entities" : qUnion([Q0]), "thickness" : 1.57 * mm});
        }
        {
            var Q0;
            Q0=makeQuery(id+"F4.opShell","OFFSET_FACE",FACE,{"disambiguationData":[OSD([sQuery(id+"F0.wireOp",EDGE,"E0.rect.bottom"),sQuery(id+"F0.wireOp",EDGE,"E0.rect.top"),sQuery(id+"F0.wireOp",EDGE,"E0.rect.left"),sQuery(id+"F0.wireOp",EDGE,"E0.rect.right")])]});
            var sketch = newSketch(context, id + "F5", { "sketchPlane" : qUnion([Q0])});
            skCircle(sketch, "E78", {"center": v(-7.87, 7.87) * mm, "radius": 2.46 * mm});
            skCircle(sketch, "E79", {"center": v(-15.75, 7.87) * mm, "radius": 2.46 * mm});
            skCircle(sketch, "E80", {"center": v(0, 7.87) * mm, "radius": 2.46 * mm});
            skCircle(sketch, "E81", {"center": v(7.87, 7.87) * mm, "radius": 2.46 * mm});
            skCircle(sketch, "E82", {"center": v(15.75, 7.87) * mm, "radius": 2.46 * mm});
            skCircle(sketch, "E83", {"center": v(15.75, 0) * mm, "radius": 2.46 * mm});
            skCircle(sketch, "E84", {"center": v(7.87, 0) * mm, "radius": 2.46 * mm});
            skCircle(sketch, "E85", {"center": v(0, 0) * mm, "radius": 2.46 * mm});
            skCircle(sketch, "E86", {"center": v(-7.87, 0) * mm, "radius": 2.46 * mm});
            skCircle(sketch, "E87", {"center": v(-15.75, 0) * mm, "radius": 2.46 * mm});
            skCircle(sketch, "E88", {"center": v(-15.75, -7.87) * mm, "radius": 2.46 * mm});
            skCircle(sketch, "E89", {"center": v(-7.87, -7.87) * mm, "radius": 2.46 * mm});
            skCircle(sketch, "E90", {"center": v(0, -7.87) * mm, "radius": 2.46 * mm});
            skCircle(sketch, "E91", {"center": v(7.87, -7.87) * mm, "radius": 2.46 * mm});
            skCircle(sketch, "E92", {"center": v(15.75, -7.87) * mm, "radius": 2.46 * mm});
            skCircle(sketch, "E93", {"center": v(-15.75, 7.87) * mm, "radius": 3.18 * mm});
            skCircle(sketch, "E94", {"center": v(-7.87, 7.87) * mm, "radius": 3.18 * mm});
            skCircle(sketch, "E95", {"center": v(0, 7.87) * mm, "radius": 3.18 * mm});
            skCircle(sketch, "E96", {"center": v(7.87, 7.87) * mm, "radius": 3.18 * mm});
            skCircle(sketch, "E97", {"center": v(15.75, 7.87) * mm, "radius": 3.18 * mm});
            skCircle(sketch, "E98", {"center": v(15.75, 0) * mm, "radius": 3.18 * mm});
            skCircle(sketch, "E99", {"center": v(7.87, 0) * mm, "radius": 3.18 * mm});
            skCircle(sketch, "E100", {"center": v(0, 0) * mm, "radius": 3.18 * mm});
            skCircle(sketch, "E101", {"center": v(-7.87, 0) * mm, "radius": 3.18 * mm});
            skCircle(sketch, "E102", {"center": v(-15.75, 0) * mm, "radius": 3.18 * mm});
            skCircle(sketch, "E103", {"center": v(-15.75, -7.87) * mm, "radius": 3.18 * mm});
            skCircle(sketch, "E104", {"center": v(-7.87, -7.87) * mm, "radius": 3.18 * mm});
            skCircle(sketch, "E105", {"center": v(0, -7.87) * mm, "radius": 3.18 * mm});
            skCircle(sketch, "E106", {"center": v(7.87, -7.87) * mm, "radius": 3.18 * mm});
            skCircle(sketch, "E107", {"center": v(15.75, -7.87) * mm, "radius": 3.18 * mm});
            skLineSegment(sketch, "E108", {"start": v(-3.94, -11.81) * mm, "end": v(3.94, -11.81) * mm});
            skLineSegment(sketch, "E109", {"start": v(-3.94, 11.81) * mm, "end": v(3.94, 11.81) * mm});
            skCircle(sketch, "E110.MirrorC", {"center": v(15.75, -15.75) * mm, "radius": 2.46 * mm});
            skCircle(sketch, "E111.MirrorC", {"center": v(0, -15.75) * mm, "radius": 3.18 * mm});
            skCircle(sketch, "E112.MirrorC", {"center": v(15.75, -15.75) * mm, "radius": 3.18 * mm});
            skCircle(sketch, "E113.MirrorC", {"center": v(-15.75, -15.75) * mm, "radius": 2.46 * mm});
            skCircle(sketch, "E114.MirrorC", {"center": v(0, -15.75) * mm, "radius": 2.46 * mm});
            skCircle(sketch, "E115.MirrorC", {"center": v(-7.87, -15.75) * mm, "radius": 3.18 * mm});
            skCircle(sketch, "E116.MirrorC", {"center": v(-7.87, -15.75) * mm, "radius": 2.46 * mm});
            skCircle(sketch, "E117.MirrorC", {"center": v(7.87, -15.75) * mm, "radius": 2.46 * mm});
            skCircle(sketch, "E118.MirrorC", {"center": v(7.87, -15.75) * mm, "radius": 3.18 * mm});
            skCircle(sketch, "E119.MirrorC", {"center": v(-15.75, -15.75) * mm, "radius": 3.18 * mm});
            skCircle(sketch, "E120.MirrorC", {"center": v(-7.87, 15.75) * mm, "radius": 3.18 * mm});
            skCircle(sketch, "E121.MirrorC", {"center": v(7.87, 15.75) * mm, "radius": 2.46 * mm});
            skCircle(sketch, "E122.MirrorC", {"center": v(15.75, 15.75) * mm, "radius": 3.18 * mm});
            skCircle(sketch, "E123.MirrorC", {"center": v(0, 15.75) * mm, "radius": 3.18 * mm});
            skCircle(sketch, "E124.MirrorC", {"center": v(15.75, 15.75) * mm, "radius": 2.46 * mm});
            skCircle(sketch, "E125.MirrorC", {"center": v(7.87, 15.75) * mm, "radius": 3.18 * mm});
            skCircle(sketch, "E126.MirrorC", {"center": v(-7.87, 15.75) * mm, "radius": 2.46 * mm});
            skCircle(sketch, "E127.MirrorC", {"center": v(0, 15.75) * mm, "radius": 2.46 * mm});
            skCircle(sketch, "E128.MirrorC", {"center": v(-15.75, 15.75) * mm, "radius": 3.18 * mm});
            skCircle(sketch, "E129.MirrorC", {"center": v(-15.75, 15.75) * mm, "radius": 2.46 * mm});
            skSolve(sketch);
        }
        {
            var Q0;
            Q0=makeQuery(id+"F5.imprint","IMPRINT",FACE,{"disambiguationData":[TD([[makeQuery(id+"F5.imprint","IMPRINT",EDGE,{"derivedFrom":sQuery(id+"F5.wireOp",EDGE,"E79")}),-1.0]])]});
            var Q1;
            Q1=makeQuery(id+"F5.imprint","IMPRINT",FACE,{"disambiguationData":[TD([[makeQuery(id+"F5.imprint","IMPRINT",EDGE,{"derivedFrom":sQuery(id+"F5.wireOp",EDGE,"E78")}),-1.0]])]});
            var Q2;
            Q2=makeQuery(id+"F5.imprint","IMPRINT",FACE,{"disambiguationData":[TD([[makeQuery(id+"F5.imprint","IMPRINT",EDGE,{"derivedFrom":sQuery(id+"F5.wireOp",EDGE,"E80")}),-1.0]])]});
            var Q3;
            Q3=makeQuery(id+"F5.imprint","IMPRINT",FACE,{"disambiguationData":[TD([[makeQuery(id+"F5.imprint","IMPRINT",EDGE,{"derivedFrom":sQuery(id+"F5.wireOp",EDGE,"E81")}),-1.0]])]});
            var Q4;
            Q4=makeQuery(id+"F5.imprint","IMPRINT",FACE,{"disambiguationData":[TD([[makeQuery(id+"F5.imprint","IMPRINT",EDGE,{"derivedFrom":sQuery(id+"F5.wireOp",EDGE,"E82")}),-1.0]])]});
            var Q5;
            Q5=makeQuery(id+"F5.imprint","IMPRINT",FACE,{"disambiguationData":[TD([[makeQuery(id+"F5.imprint","IMPRINT",EDGE,{"derivedFrom":sQuery(id+"F5.wireOp",EDGE,"E83")}),-1.0]])]});
            var Q6;
            Q6=makeQuery(id+"F5.imprint","IMPRINT",FACE,{"disambiguationData":[TD([[makeQuery(id+"F5.imprint","IMPRINT",EDGE,{"derivedFrom":sQuery(id+"F5.wireOp",EDGE,"E84")}),-1.0]])]});
            var Q7;
            Q7=makeQuery(id+"F5.imprint","IMPRINT",FACE,{"disambiguationData":[TD([[makeQuery(id+"F5.imprint","IMPRINT",EDGE,{"derivedFrom":sQuery(id+"F5.wireOp",EDGE,"E85")}),-1.0]])]});
            var Q8;
            Q8=makeQuery(id+"F5.imprint","IMPRINT",FACE,{"disambiguationData":[TD([[makeQuery(id+"F5.imprint","IMPRINT",EDGE,{"derivedFrom":sQuery(id+"F5.wireOp",EDGE,"E86")}),-1.0]])]});
            var Q9;
            Q9=makeQuery(id+"F5.imprint","IMPRINT",FACE,{"disambiguationData":[TD([[makeQuery(id+"F5.imprint","IMPRINT",EDGE,{"derivedFrom":sQuery(id+"F5.wireOp",EDGE,"E87")}),-1.0]])]});
            var Q10;
            Q10=makeQuery(id+"F5.imprint","IMPRINT",FACE,{"disambiguationData":[TD([[makeQuery(id+"F5.imprint","IMPRINT",EDGE,{"derivedFrom":sQuery(id+"F5.wireOp",EDGE,"E88")}),-1.0]])]});
            var Q11;
            Q11=makeQuery(id+"F5.imprint","IMPRINT",FACE,{"disambiguationData":[TD([[makeQuery(id+"F5.imprint","IMPRINT",EDGE,{"derivedFrom":sQuery(id+"F5.wireOp",EDGE,"E89")}),-1.0]])]});
            var Q12;
            Q12=makeQuery(id+"F5.imprint","IMPRINT",FACE,{"disambiguationData":[TD([[makeQuery(id+"F5.imprint","IMPRINT",EDGE,{"derivedFrom":sQuery(id+"F5.wireOp",EDGE,"E90")}),-1.0]])]});
            var Q13;
            Q13=makeQuery(id+"F5.imprint","IMPRINT",FACE,{"disambiguationData":[TD([[makeQuery(id+"F5.imprint","IMPRINT",EDGE,{"derivedFrom":sQuery(id+"F5.wireOp",EDGE,"E91")}),-1.0]])]});
            var Q14;
            Q14=makeQuery(id+"F5.imprint","IMPRINT",FACE,{"disambiguationData":[TD([[makeQuery(id+"F5.imprint","IMPRINT",EDGE,{"derivedFrom":sQuery(id+"F5.wireOp",EDGE,"E92")}),-1.0]])]});
            var Q15;
            Q15=makeQuery(id+"F5.imprint","IMPRINT",FACE,{"disambiguationData":[TD([[makeQuery(id+"F5.imprint","IMPRINT",EDGE,{"derivedFrom":sQuery(id+"F5.wireOp",EDGE,"E128.MirrorC")}),-1.0]])]});
            var Q16;
            Q16=makeQuery(id+"F5.imprint","IMPRINT",FACE,{"disambiguationData":[TD([[makeQuery(id+"F5.imprint","IMPRINT",EDGE,{"derivedFrom":sQuery(id+"F5.wireOp",EDGE,"E120.MirrorC")}),-1.0]])]});
            var Q17;
            Q17=makeQuery(id+"F5.imprint","IMPRINT",FACE,{"disambiguationData":[TD([[makeQuery(id+"F5.imprint","IMPRINT",EDGE,{"derivedFrom":sQuery(id+"F5.wireOp",EDGE,"E123.MirrorC")}),-1.0]])]});
            var Q18;
            Q18=makeQuery(id+"F5.imprint","IMPRINT",FACE,{"disambiguationData":[TD([[makeQuery(id+"F5.imprint","IMPRINT",EDGE,{"derivedFrom":sQuery(id+"F5.wireOp",EDGE,"E121.MirrorC")}),1.0]])]});
            var Q19;
            Q19=makeQuery(id+"F5.imprint","IMPRINT",FACE,{"disambiguationData":[TD([[makeQuery(id+"F5.imprint","IMPRINT",EDGE,{"derivedFrom":sQuery(id+"F5.wireOp",EDGE,"E122.MirrorC")}),-1.0]])]});
            var Q20;
            Q20=makeQuery(id+"F5.imprint","IMPRINT",FACE,{"disambiguationData":[TD([[makeQuery(id+"F5.imprint","IMPRINT",EDGE,{"derivedFrom":sQuery(id+"F5.wireOp",EDGE,"E113.MirrorC")}),1.0]])]});
            var Q21;
            Q21=makeQuery(id+"F5.imprint","IMPRINT",FACE,{"disambiguationData":[TD([[makeQuery(id+"F5.imprint","IMPRINT",EDGE,{"derivedFrom":sQuery(id+"F5.wireOp",EDGE,"E115.MirrorC")}),-1.0]])]});
            var Q22;
            Q22=makeQuery(id+"F5.imprint","IMPRINT",FACE,{"disambiguationData":[TD([[makeQuery(id+"F5.imprint","IMPRINT",EDGE,{"derivedFrom":sQuery(id+"F5.wireOp",EDGE,"E111.MirrorC")}),-1.0]])]});
            var Q23;
            Q23=makeQuery(id+"F5.imprint","IMPRINT",FACE,{"disambiguationData":[TD([[makeQuery(id+"F5.imprint","IMPRINT",EDGE,{"derivedFrom":sQuery(id+"F5.wireOp",EDGE,"E117.MirrorC")}),1.0]])]});
            var Q24;
            Q24=makeQuery(id+"F5.imprint","IMPRINT",FACE,{"disambiguationData":[TD([[makeQuery(id+"F5.imprint","IMPRINT",EDGE,{"derivedFrom":sQuery(id+"F5.wireOp",EDGE,"E110.MirrorC")}),1.0]])]});
            extrude(context, id + "F6", {"entities" : qUnion([Q0, Q1, Q2, Q3, Q4, Q5, Q6, Q7, Q8, Q9, Q10, Q11, Q12, Q13, Q14, Q15, Q16, Q17, Q18, Q19, Q20, Q21, Q22, Q23, Q24]), "operationType" : NewBodyOperationType.ADD, "depth" : 1.63 * mm});
        }
    });
